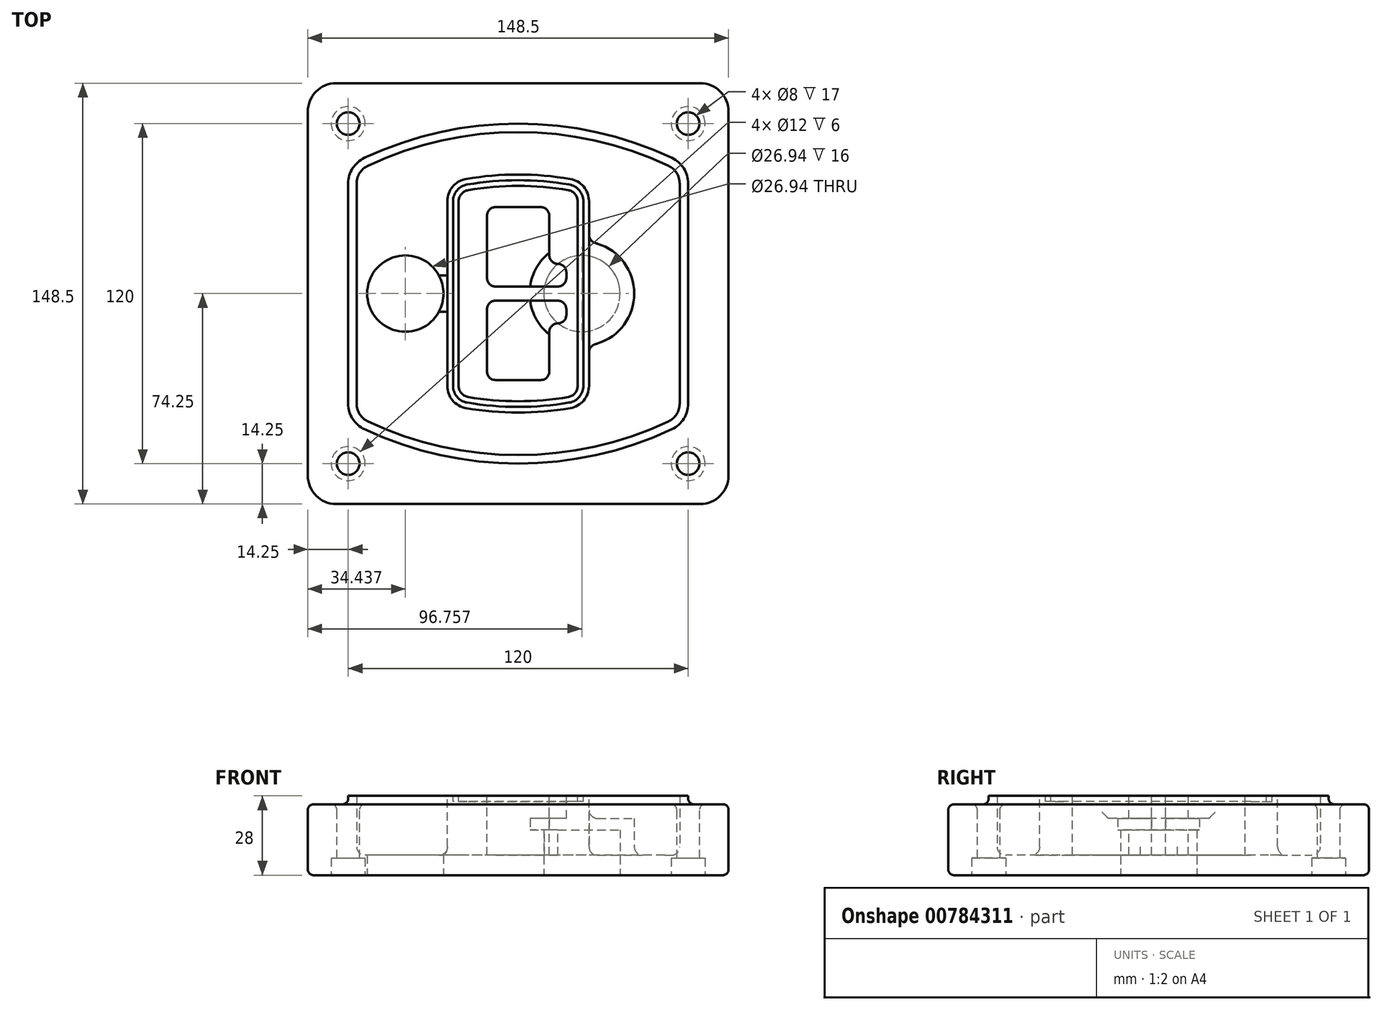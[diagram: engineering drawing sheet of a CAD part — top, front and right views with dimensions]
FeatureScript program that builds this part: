
annotation { "Feature Type Name" : "Feature", "Feature Type Description" : "" }
export const myFeature = defineFeature(function(context is Context, id is Id, definition is map)
    precondition{}
    {
        {
            var Q0;
            Q0=qCreatedBy(makeId("Top.planeOp"),FACE);
            var sketch = newSketch(context, id + "F0", { "sketchPlane" : qUnion([Q0])});
            skPoint(sketch, "E0.rect.middle", {"position": v(0, 0) * mm});
            skLineSegment(sketch, "E1.bottom", {"start": v(-64.25, -74.25) * mm, "end": v(64.25, -74.25) * mm});
            skLineSegment(sketch, "E1.top", {"start": v(-64.25, 74.25) * mm, "end": v(64.25, 74.25) * mm});
            skLineSegment(sketch, "E1.left", {"start": v(-74.25, -64.25) * mm, "end": v(-74.25, 64.25) * mm});
            skLineSegment(sketch, "E1.right", {"start": v(74.25, -64.25) * mm, "end": v(74.25, 64.25) * mm});
            skLineSegment(sketch, "E2", {"start": v(-74.25, 74.25) * mm, "end": v(74.25, -74.25) * mm, "construction": true});
            skLineSegment(sketch, "E3", {"start": v(74.25, 74.25) * mm, "end": v(-74.25, -74.25) * mm, "construction": true});
            skCircle(sketch, "E4", {"center": v(-60, 60) * mm, "radius": 4 * mm});
            skCircle(sketch, "E5", {"center": v(60, 60) * mm, "radius": 4 * mm});
            skCircle(sketch, "E6", {"center": v(60, -60) * mm, "radius": 4 * mm});
            skCircle(sketch, "E7", {"center": v(-60, -60) * mm, "radius": 4 * mm});
            skLineSegment(sketch, "E8", {"start": v(-60, 60) * mm, "end": v(60, 60) * mm, "construction": true});
            skLineSegment(sketch, "E9", {"start": v(60, 60) * mm, "end": v(60, -60) * mm, "construction": true});
            skLineSegment(sketch, "E10", {"start": v(60, -60) * mm, "end": v(-60, -60) * mm, "construction": true});
            skLineSegment(sketch, "E11", {"start": v(-60, -60) * mm, "end": v(-60, 60) * mm, "construction": true});
            skLineSegment(sketch, "E12", {"start": v(-60, 38.83) * mm, "end": v(-60, -38.83) * mm});
            skLineSegment(sketch, "E13", {"start": v(60, 38.83) * mm, "end": v(60, -38.83) * mm});
            skArc(sketch, "E14", {"start": v(54.26, 47.88) * mm, "mid": v(0, 60) * mm, "end": v(-54.26, 47.88) * mm});
            skArc(sketch, "E15", {"start": v(-54.26, -47.88) * mm, "mid": v(0, -60) * mm, "end": v(54.26, -47.88) * mm});
            skLineSegment(sketch, "E16", {"start": v(-60, 0) * mm, "end": v(60, 0) * mm, "construction": true});
            skPoint(sketch, "E17.visualSharp", {"position": v(-60, -45) * mm});
            skArc(sketch, "E17.filletArc", {"start": v(-60, -38.83) * mm, "mid": v(-58.44, -44.2) * mm, "end": v(-54.26, -47.88) * mm});
            skPoint(sketch, "E18.visualSharp", {"position": v(-60, 45) * mm});
            skArc(sketch, "E18.filletArc", {"start": v(-54.26, 47.88) * mm, "mid": v(-58.44, 44.2) * mm, "end": v(-60, 38.83) * mm});
            skPoint(sketch, "E19.visualSharp", {"position": v(60, 45) * mm});
            skArc(sketch, "E19.filletArc", {"start": v(60, 38.83) * mm, "mid": v(58.44, 44.2) * mm, "end": v(54.26, 47.88) * mm});
            skPoint(sketch, "E20.visualSharp", {"position": v(60, -45) * mm});
            skArc(sketch, "E20.filletArc", {"start": v(54.26, -47.88) * mm, "mid": v(58.44, -44.2) * mm, "end": v(60, -38.83) * mm});
            skPoint(sketch, "E21.visualSharp", {"position": v(-74.25, 74.25) * mm});
            skArc(sketch, "E21.filletArc", {"start": v(-64.25, 74.25) * mm, "mid": v(-71.32, 71.32) * mm, "end": v(-74.25, 64.25) * mm});
            skPoint(sketch, "E22.visualSharp", {"position": v(74.25, 74.25) * mm});
            skArc(sketch, "E22.filletArc", {"start": v(74.25, 64.25) * mm, "mid": v(71.32, 71.32) * mm, "end": v(64.25, 74.25) * mm});
            skPoint(sketch, "E23.visualSharp", {"position": v(74.25, -74.25) * mm});
            skArc(sketch, "E23.filletArc", {"start": v(64.25, -74.25) * mm, "mid": v(71.32, -71.32) * mm, "end": v(74.25, -64.25) * mm});
            skPoint(sketch, "E24.visualSharp", {"position": v(-74.25, -74.25) * mm});
            skArc(sketch, "E24.filletArc", {"start": v(-74.25, -64.25) * mm, "mid": v(-71.32, -71.32) * mm, "end": v(-64.25, -74.25) * mm});
            skArc(sketch, "E25.0", {"start": v(57, 38.83) * mm, "mid": v(55.9, 42.58) * mm, "end": v(52.98, 45.17) * mm});
            skLineSegment(sketch, "E25.1", {"start": v(57, 38.83) * mm, "end": v(57, -38.83) * mm});
            skArc(sketch, "E25.2", {"start": v(52.98, -45.17) * mm, "mid": v(55.9, -42.58) * mm, "end": v(57, -38.83) * mm});
            skArc(sketch, "E25.3", {"start": v(-52.98, -45.17) * mm, "mid": v(0, -57) * mm, "end": v(52.98, -45.17) * mm});
            skArc(sketch, "E25.4", {"start": v(-57, -38.83) * mm, "mid": v(-55.9, -42.58) * mm, "end": v(-52.98, -45.17) * mm});
            skArc(sketch, "E25.5", {"start": v(52.98, 45.17) * mm, "mid": v(0, 57) * mm, "end": v(-52.98, 45.17) * mm});
            skLineSegment(sketch, "E25.6", {"start": v(-57, 38.83) * mm, "end": v(-57, -38.83) * mm});
            skArc(sketch, "E25.7", {"start": v(-52.98, 45.17) * mm, "mid": v(-55.9, 42.58) * mm, "end": v(-57, 38.83) * mm});
            skArc(sketch, "E26.0", {"start": v(-55.96, 51.5) * mm, "mid": v(-61.82, 46.33) * mm, "end": v(-64, 38.83) * mm});
            skArc(sketch, "E26.1", {"start": v(55.96, 51.5) * mm, "mid": v(0, 64) * mm, "end": v(-55.96, 51.5) * mm});
            skArc(sketch, "E26.2", {"start": v(64, 38.83) * mm, "mid": v(61.82, 46.33) * mm, "end": v(55.96, 51.5) * mm});
            skLineSegment(sketch, "E26.3", {"start": v(64, 38.83) * mm, "end": v(64, -38.83) * mm});
            skArc(sketch, "E26.4", {"start": v(55.96, -51.5) * mm, "mid": v(61.82, -46.33) * mm, "end": v(64, -38.83) * mm});
            skLineSegment(sketch, "E26.5", {"start": v(-64, 38.83) * mm, "end": v(-64, -38.83) * mm});
            skArc(sketch, "E26.6", {"start": v(-55.96, -51.5) * mm, "mid": v(0, -64) * mm, "end": v(55.96, -51.5) * mm});
            skArc(sketch, "E26.7", {"start": v(-64, -38.83) * mm, "mid": v(-61.82, -46.33) * mm, "end": v(-55.96, -51.5) * mm});
            skSolve(sketch);
        }
        {
            var Q0;
            Q0=makeQuery(id+"F0.imprint","IMPRINT",FACE,{"disambiguationData":[TD([[makeQuery(id+"F0.imprint","IMPRINT",EDGE,{"derivedFrom":sQuery(id+"F0.wireOp",EDGE,"E1.bottom")}),1.0]])]});
            var Q1;
            Q1=makeQuery(id+"F0.imprint","IMPRINT",FACE,{"disambiguationData":[TD([[makeQuery(id+"F0.imprint","IMPRINT",EDGE,{"derivedFrom":sQuery(id+"F0.wireOp",EDGE,"E12")}),1.0]])]});
            var Q2;
            Q2=makeQuery(id+"F0.imprint","IMPRINT",FACE,{"disambiguationData":[TD([[makeQuery(id+"F0.imprint","IMPRINT",EDGE,{"derivedFrom":sQuery(id+"F0.wireOp",EDGE,"E25.0")}),1.0]])]});
            var Q3;
            Q3=makeQuery(id+"F0.imprint","IMPRINT",FACE,{"disambiguationData":[TD([[makeQuery(id+"F0.imprint","IMPRINT",EDGE,{"derivedFrom":sQuery(id+"F0.wireOp",EDGE,"E12")}),-1.0]])]});
            extrude(context, id + "F1", {"entities" : qUnion([Q0, Q1, Q2, Q3]), "oppositeDirection" : true, "depth" : 25 * mm});
        }
        {
            var Q0;
            Q0=makeQuery(id+"F0.imprint","IMPRINT",FACE,{"disambiguationData":[TD([[makeQuery(id+"F0.imprint","IMPRINT",EDGE,{"derivedFrom":sQuery(id+"F0.wireOp",EDGE,"E12")}),1.0]])]});
            extrude(context, id + "F2", {"entities" : qUnion([Q0]), "operationType" : NewBodyOperationType.ADD, "depth" : 3 * mm});
        }
        {
            var Q0;
            Q0=makeQuery(id+"F0.imprint","IMPRINT",FACE,{"disambiguationData":[TD([[makeQuery(id+"F0.imprint","IMPRINT",EDGE,{"derivedFrom":sQuery(id+"F0.wireOp",EDGE,"E25.0")}),1.0]])]});
            extrude(context, id + "F3", {"entities" : qUnion([Q0]), "operationType" : NewBodyOperationType.REMOVE, "oppositeDirection" : true, "depth" : 18 * mm});
        }
        {
            var Q0;
            Q0=makeQuery(id+"F2.opExtrude","CAP_FACE",FACE,{"disambiguationData":[OSD([sQuery(id+"F0.wireOp",EDGE,"E12"),sQuery(id+"F0.wireOp",EDGE,"E13"),sQuery(id+"F0.wireOp",EDGE,"E14"),sQuery(id+"F0.wireOp",EDGE,"E15"),sQuery(id+"F0.wireOp",EDGE,"E17.filletArc"),sQuery(id+"F0.wireOp",EDGE,"E18.filletArc"),sQuery(id+"F0.wireOp",EDGE,"E19.filletArc"),sQuery(id+"F0.wireOp",EDGE,"E20.filletArc"),sQuery(id+"F0.wireOp",EDGE,"E25.0"),sQuery(id+"F0.wireOp",EDGE,"E25.1"),sQuery(id+"F0.wireOp",EDGE,"E25.2"),sQuery(id+"F0.wireOp",EDGE,"E25.3"),sQuery(id+"F0.wireOp",EDGE,"E25.4"),sQuery(id+"F0.wireOp",EDGE,"E25.5"),sQuery(id+"F0.wireOp",EDGE,"E25.6"),sQuery(id+"F0.wireOp",EDGE,"E25.7")])],"isStart":false});
            var sketch = newSketch(context, id + "F4", { "sketchPlane" : qUnion([Q0])});
            skArc(sketch, "E27.0", {"start": v(-18.34, -40.45) * mm, "mid": v(0, -42) * mm, "end": v(18.34, -40.45) * mm});
            skArc(sketch, "E28.0", {"start": v(18.34, 40.45) * mm, "mid": v(0, 42) * mm, "end": v(-18.34, 40.45) * mm});
            skLineSegment(sketch, "E29", {"start": v(-25, 32.57) * mm, "end": v(-25, -32.57) * mm});
            skLineSegment(sketch, "E30", {"start": v(25, 32.57) * mm, "end": v(25, -32.57) * mm});
            skLineSegment(sketch, "E31", {"start": v(-25, 39.1) * mm, "end": v(25, 39.1) * mm, "construction": true});
            skLineSegment(sketch, "E32", {"start": v(-25, -39.1) * mm, "end": v(25, -39.1) * mm, "construction": true});
            skPoint(sketch, "E33.visualSharp", {"position": v(-25, 39.1) * mm});
            skArc(sketch, "E33.filletArc", {"start": v(-18.34, 40.45) * mm, "mid": v(-23.11, 37.73) * mm, "end": v(-25, 32.57) * mm});
            skPoint(sketch, "E34.visualSharp", {"position": v(25, 39.1) * mm});
            skArc(sketch, "E34.filletArc", {"start": v(25, 32.57) * mm, "mid": v(23.11, 37.73) * mm, "end": v(18.34, 40.45) * mm});
            skPoint(sketch, "E35.visualSharp", {"position": v(25, -39.1) * mm});
            skArc(sketch, "E35.filletArc", {"start": v(18.34, -40.45) * mm, "mid": v(23.11, -37.73) * mm, "end": v(25, -32.57) * mm});
            skPoint(sketch, "E36.visualSharp", {"position": v(-25, -39.1) * mm});
            skArc(sketch, "E36.filletArc", {"start": v(-25, -32.57) * mm, "mid": v(-23.11, -37.73) * mm, "end": v(-18.34, -40.45) * mm});
            skArc(sketch, "E37.0", {"start": v(52.98, 45.17) * mm, "mid": v(0, 57) * mm, "end": v(-52.98, 45.17) * mm});
            skArc(sketch, "E37.1", {"start": v(-52.98, 45.17) * mm, "mid": v(-55.9, 42.58) * mm, "end": v(-57, 38.83) * mm});
            skLineSegment(sketch, "E37.2", {"start": v(-57, 38.83) * mm, "end": v(-57, -38.83) * mm});
            skArc(sketch, "E37.3", {"start": v(-57, -38.83) * mm, "mid": v(-55.9, -42.58) * mm, "end": v(-52.98, -45.17) * mm});
            skArc(sketch, "E37.4", {"start": v(-52.98, -45.17) * mm, "mid": v(0, -57) * mm, "end": v(52.98, -45.17) * mm});
            skArc(sketch, "E37.5", {"start": v(52.98, -45.17) * mm, "mid": v(55.9, -42.58) * mm, "end": v(57, -38.83) * mm});
            skLineSegment(sketch, "E37.6", {"start": v(57, 38.83) * mm, "end": v(57, -38.83) * mm});
            skArc(sketch, "E37.7", {"start": v(57, 38.83) * mm, "mid": v(55.9, 42.58) * mm, "end": v(52.98, 45.17) * mm});
            skLineSegment(sketch, "E38.0", {"start": v(23, 32.57) * mm, "end": v(23, -32.57) * mm});
            skArc(sketch, "E38.1", {"start": v(18, -38.48) * mm, "mid": v(21.58, -36.44) * mm, "end": v(23, -32.57) * mm});
            skArc(sketch, "E38.2", {"start": v(-18, -38.48) * mm, "mid": v(0, -40) * mm, "end": v(18, -38.48) * mm});
            skArc(sketch, "E38.3", {"start": v(-23, -32.57) * mm, "mid": v(-21.58, -36.44) * mm, "end": v(-18, -38.48) * mm});
            skLineSegment(sketch, "E38.4", {"start": v(-23, 32.57) * mm, "end": v(-23, -32.57) * mm});
            skArc(sketch, "E38.5", {"start": v(23, 32.57) * mm, "mid": v(21.58, 36.44) * mm, "end": v(18, 38.48) * mm});
            skArc(sketch, "E38.6", {"start": v(-18, 38.48) * mm, "mid": v(-21.58, 36.44) * mm, "end": v(-23, 32.57) * mm});
            skArc(sketch, "E38.7", {"start": v(18, 38.48) * mm, "mid": v(0, 40) * mm, "end": v(-18, 38.48) * mm});
            skArc(sketch, "E39.0", {"start": v(21, 32.57) * mm, "mid": v(20.06, 35.15) * mm, "end": v(17.67, 36.5) * mm});
            skLineSegment(sketch, "E39.1", {"start": v(21, 32.57) * mm, "end": v(21, -32.57) * mm});
            skArc(sketch, "E39.2", {"start": v(17.67, -36.5) * mm, "mid": v(20.06, -35.15) * mm, "end": v(21, -32.57) * mm});
            skArc(sketch, "E39.3", {"start": v(-17.67, -36.5) * mm, "mid": v(0, -38) * mm, "end": v(17.67, -36.5) * mm});
            skArc(sketch, "E39.4", {"start": v(-21, -32.57) * mm, "mid": v(-20.06, -35.15) * mm, "end": v(-17.67, -36.5) * mm});
            skArc(sketch, "E39.5", {"start": v(17.67, 36.5) * mm, "mid": v(0, 38) * mm, "end": v(-17.67, 36.5) * mm});
            skLineSegment(sketch, "E39.6", {"start": v(-21, 32.57) * mm, "end": v(-21, -32.57) * mm});
            skArc(sketch, "E39.7", {"start": v(-17.67, 36.5) * mm, "mid": v(-20.06, 35.15) * mm, "end": v(-21, 32.57) * mm});
            skLineSegment(sketch, "E40", {"start": v(-25, 0) * mm, "end": v(25, 0) * mm, "construction": true});
            skLineSegment(sketch, "E41", {"start": v(-11, 5.5) * mm, "end": v(-11, 27.5) * mm});
            skLineSegment(sketch, "E42", {"start": v(-8, 30.5) * mm, "end": v(8, 30.5) * mm});
            skLineSegment(sketch, "E43", {"start": v(11, 27.5) * mm, "end": v(11, 13.5) * mm});
            skLineSegment(sketch, "E44", {"start": v(14, 10.5) * mm, "end": v(14, 10.5) * mm});
            skLineSegment(sketch, "E45", {"start": v(17, 7.5) * mm, "end": v(17, 5.5) * mm});
            skLineSegment(sketch, "E46", {"start": v(14, 2.5) * mm, "end": v(-8, 2.5) * mm});
            skPoint(sketch, "E47.visualSharp", {"position": v(-11, 30.5) * mm});
            skArc(sketch, "E47.filletArc", {"start": v(-8, 30.5) * mm, "mid": v(-10.12, 29.62) * mm, "end": v(-11, 27.5) * mm});
            skPoint(sketch, "E48.visualSharp", {"position": v(11, 30.5) * mm});
            skArc(sketch, "E48.filletArc", {"start": v(11, 27.5) * mm, "mid": v(10.12, 29.62) * mm, "end": v(8, 30.5) * mm});
            skPoint(sketch, "E49.visualSharp", {"position": v(11, 10.5) * mm});
            skArc(sketch, "E49.filletArc", {"start": v(11, 13.5) * mm, "mid": v(11.88, 11.38) * mm, "end": v(14, 10.5) * mm});
            skPoint(sketch, "E50.visualSharp", {"position": v(17, 10.5) * mm});
            skArc(sketch, "E50.filletArc", {"start": v(17, 7.5) * mm, "mid": v(16.12, 9.62) * mm, "end": v(14, 10.5) * mm});
            skPoint(sketch, "E51.visualSharp", {"position": v(17, 2.5) * mm});
            skArc(sketch, "E51.filletArc", {"start": v(14, 2.5) * mm, "mid": v(16.12, 3.38) * mm, "end": v(17, 5.5) * mm});
            skPoint(sketch, "E52.visualSharp", {"position": v(-11, 2.5) * mm});
            skArc(sketch, "E52.filletArc", {"start": v(-11, 5.5) * mm, "mid": v(-10.12, 3.38) * mm, "end": v(-8, 2.5) * mm});
            skLineSegment(sketch, "E53.0.MirrorCS", {"start": v(14, -2.5) * mm, "end": v(-8, -2.5) * mm});
            skArc(sketch, "E54.0.MirrorCS", {"start": v(-11, -5.5) * mm, "mid": v(-10.12, -3.38) * mm, "end": v(-8, -2.5) * mm});
            skLineSegment(sketch, "E55.0.MirrorCS", {"start": v(-11, -5.5) * mm, "end": v(-11, -27.5) * mm});
            skArc(sketch, "E56.0.MirrorCS", {"start": v(-8, -30.5) * mm, "mid": v(-10.12, -29.62) * mm, "end": v(-11, -27.5) * mm});
            skLineSegment(sketch, "E57.0.MirrorCS", {"start": v(-8, -30.5) * mm, "end": v(8, -30.5) * mm});
            skArc(sketch, "E58.0.MirrorCS", {"start": v(11, -27.5) * mm, "mid": v(10.12, -29.62) * mm, "end": v(8, -30.5) * mm});
            skLineSegment(sketch, "E59.0.MirrorCS", {"start": v(11, -27.5) * mm, "end": v(11, -13.5) * mm});
            skArc(sketch, "E60.0.MirrorCS", {"start": v(11, -13.5) * mm, "mid": v(11.88, -11.38) * mm, "end": v(14, -10.5) * mm});
            skArc(sketch, "E61.0.MirrorCS", {"start": v(17, -7.5) * mm, "mid": v(16.12, -9.62) * mm, "end": v(14, -10.5) * mm});
            skLineSegment(sketch, "E62.0.MirrorCS", {"start": v(17, -7.5) * mm, "end": v(17, -5.5) * mm});
            skArc(sketch, "E63.0.MirrorCS", {"start": v(14, -2.5) * mm, "mid": v(16.12, -3.38) * mm, "end": v(17, -5.5) * mm});
            skSolve(sketch);
        }
        {
            var Q0;
            Q0=makeQuery(id+"F4.imprint","IMPRINT",FACE,{"disambiguationData":[TD([[makeQuery(id+"F4.imprint","IMPRINT",EDGE,{"derivedFrom":sQuery(id+"F4.wireOp",EDGE,"E27.0")}),1.0]])]});
            var Q1;
            Q1=makeQuery(id+"F4.imprint","IMPRINT",FACE,{"disambiguationData":[TD([[makeQuery(id+"F4.imprint","IMPRINT",EDGE,{"derivedFrom":sQuery(id+"F4.wireOp",EDGE,"E38.0")}),-1.0]])]});
            var Q2;
            Q2=makeQuery(id+"F4.imprint","IMPRINT",FACE,{"disambiguationData":[TD([[makeQuery(id+"F4.imprint","IMPRINT",EDGE,{"derivedFrom":sQuery(id+"F4.wireOp",EDGE,"E39.0")}),1.0]])]});
            extrude(context, id + "F5", {"entities" : qUnion([Q0, Q1, Q2]), "operationType" : NewBodyOperationType.ADD, "endBound" : BoundingType.UP_TO_NEXT, "oppositeDirection" : true, "depth" : 25 * mm});
        }
        {
            var Q0;
            Q0=makeQuery(id+"F4.imprint","IMPRINT",FACE,{"disambiguationData":[TD([[makeQuery(id+"F4.imprint","IMPRINT",EDGE,{"derivedFrom":sQuery(id+"F4.wireOp",EDGE,"E38.0")}),-1.0]])]});
            extrude(context, id + "F6", {"entities" : qUnion([Q0]), "operationType" : NewBodyOperationType.REMOVE, "oppositeDirection" : true, "depth" : 2 * mm});
        }
        {
            var Q0;
            Q0=makeQuery(id+"F1.opExtrude","CAP_FACE",FACE,{"disambiguationData":[OSD([sQuery(id+"F0.wireOp",EDGE,"E1.bottom"),sQuery(id+"F0.wireOp",EDGE,"E1.top"),sQuery(id+"F0.wireOp",EDGE,"E1.left"),sQuery(id+"F0.wireOp",EDGE,"E1.right"),sQuery(id+"F0.wireOp",EDGE,"E4"),sQuery(id+"F0.wireOp",EDGE,"E5"),sQuery(id+"F0.wireOp",EDGE,"E6"),sQuery(id+"F0.wireOp",EDGE,"E7"),sQuery(id+"F0.wireOp",EDGE,"E21.filletArc"),sQuery(id+"F0.wireOp",EDGE,"E22.filletArc"),sQuery(id+"F0.wireOp",EDGE,"E23.filletArc"),sQuery(id+"F0.wireOp",EDGE,"E24.filletArc")])],"isStart":false});
            var sketch = newSketch(context, id + "F7", { "sketchPlane" : qUnion([Q0])});
            skCircle(sketch, "E64", {"center": v(22.5, 0) * mm, "radius": 13.47 * mm});
            skCircle(sketch, "E65", {"center": v(-39.81, 0) * mm, "radius": 13.47 * mm});
            skLineSegment(sketch, "E66", {"start": v(74.25, 0) * mm, "end": v(-74.25, 0) * mm});
            skCircle(sketch, "E67", {"center": v(22.5, 0) * mm, "radius": 18.47 * mm});
            skCircle(sketch, "E68", {"center": v(60, -60) * mm, "radius": 6 * mm});
            skCircle(sketch, "E69", {"center": v(-60, -60) * mm, "radius": 6 * mm});
            skCircle(sketch, "E70", {"center": v(-60, 60) * mm, "radius": 6 * mm});
            skCircle(sketch, "E71", {"center": v(60, 60) * mm, "radius": 6 * mm});
            skSolve(sketch);
        }
        {
            var Q0;
            {var subQ1=sQuery(id+"F7.wireOp",EDGE,"E66");var subQ4=sQuery(id+"F7.wireOp",EDGE,"E64");var subQ6=makeQuery(id+"F7.imprint","INTERSECT",VERTEX,{"disambiguationData":[OD(0.0)],"derivedFrom":[subQ4,subQ1]});Q0=makeQuery(id+"F7.imprint","IMPRINT",FACE,{"disambiguationData":[TD([[makeQuery(id+"F7.imprint","IMPRINT",EDGE,{"disambiguationData":[TD([[subQ6,-1.0]])],"derivedFrom":subQ4}),-1.0]])]});}
            var Q1;
            {var subQ0=sQuery(id+"F7.wireOp",EDGE,"E66");var subQ1=sQuery(id+"F7.wireOp",EDGE,"E64");var subQ3=makeQuery(id+"F7.imprint","INTERSECT",VERTEX,{"disambiguationData":[OD(0.0)],"derivedFrom":[subQ1,subQ0]});Q1=makeQuery(id+"F7.imprint","IMPRINT",FACE,{"disambiguationData":[TD([[makeQuery(id+"F7.imprint","IMPRINT",EDGE,{"disambiguationData":[TD([[subQ3,-1.0]])],"derivedFrom":subQ1}),1.0]])]});}
            var Q2;
            {var subQ0=sQuery(id+"F7.wireOp",EDGE,"E66");var subQ1=sQuery(id+"F7.wireOp",EDGE,"E64");var subQ3=makeQuery(id+"F7.imprint","INTERSECT",VERTEX,{"disambiguationData":[OD(0.0)],"derivedFrom":[subQ1,subQ0]});Q2=makeQuery(id+"F7.imprint","IMPRINT",FACE,{"disambiguationData":[TD([[makeQuery(id+"F7.imprint","IMPRINT",EDGE,{"disambiguationData":[TD([[subQ3,1.0]])],"derivedFrom":subQ1}),1.0]])]});}
            var Q3;
            {var subQ1=sQuery(id+"F7.wireOp",EDGE,"E66");var subQ4=sQuery(id+"F7.wireOp",EDGE,"E64");var subQ6=makeQuery(id+"F7.imprint","INTERSECT",VERTEX,{"disambiguationData":[OD(0.0)],"derivedFrom":[subQ4,subQ1]});Q3=makeQuery(id+"F7.imprint","IMPRINT",FACE,{"disambiguationData":[TD([[makeQuery(id+"F7.imprint","IMPRINT",EDGE,{"disambiguationData":[TD([[subQ6,1.0]])],"derivedFrom":subQ4}),-1.0]])]});}
            extrude(context, id + "F8", {"entities" : qUnion([Q0, Q1, Q2, Q3]), "operationType" : NewBodyOperationType.ADD, "oppositeDirection" : true, "depth" : 20 * mm});
        }
        {
            var Q0;
            {var subQ0=sQuery(id+"F7.wireOp",EDGE,"E66");var subQ1=sQuery(id+"F7.wireOp",EDGE,"E64");var subQ3=makeQuery(id+"F7.imprint","INTERSECT",VERTEX,{"disambiguationData":[OD(0.0)],"derivedFrom":[subQ1,subQ0]});Q0=makeQuery(id+"F7.imprint","IMPRINT",FACE,{"disambiguationData":[TD([[makeQuery(id+"F7.imprint","IMPRINT",EDGE,{"disambiguationData":[TD([[subQ3,-1.0]])],"derivedFrom":subQ1}),1.0]])]});}
            var Q1;
            {var subQ0=sQuery(id+"F7.wireOp",EDGE,"E66");var subQ1=sQuery(id+"F7.wireOp",EDGE,"E64");var subQ3=makeQuery(id+"F7.imprint","INTERSECT",VERTEX,{"disambiguationData":[OD(0.0)],"derivedFrom":[subQ1,subQ0]});Q1=makeQuery(id+"F7.imprint","IMPRINT",FACE,{"disambiguationData":[TD([[makeQuery(id+"F7.imprint","IMPRINT",EDGE,{"disambiguationData":[TD([[subQ3,1.0]])],"derivedFrom":subQ1}),1.0]])]});}
            extrude(context, id + "F9", {"entities" : qUnion([Q0, Q1]), "operationType" : NewBodyOperationType.REMOVE, "oppositeDirection" : true, "depth" : 16 * mm});
        }
        {
            var Q0;
            {var subQ0=sQuery(id+"F7.wireOp",EDGE,"E66");var subQ1=sQuery(id+"F7.wireOp",EDGE,"E65");var subQ3=makeQuery(id+"F7.imprint","INTERSECT",VERTEX,{"disambiguationData":[OD(0.0)],"derivedFrom":[subQ1,subQ0]});Q0=makeQuery(id+"F7.imprint","IMPRINT",FACE,{"disambiguationData":[TD([[makeQuery(id+"F7.imprint","IMPRINT",EDGE,{"disambiguationData":[TD([[subQ3,-1.0]])],"derivedFrom":subQ1}),1.0]])]});}
            var Q1;
            {var subQ0=sQuery(id+"F7.wireOp",EDGE,"E66");var subQ1=sQuery(id+"F7.wireOp",EDGE,"E65");var subQ3=makeQuery(id+"F7.imprint","INTERSECT",VERTEX,{"disambiguationData":[OD(0.0)],"derivedFrom":[subQ1,subQ0]});Q1=makeQuery(id+"F7.imprint","IMPRINT",FACE,{"disambiguationData":[TD([[makeQuery(id+"F7.imprint","IMPRINT",EDGE,{"disambiguationData":[TD([[subQ3,1.0]])],"derivedFrom":subQ1}),1.0]])]});}
            extrude(context, id + "F10", {"entities" : qUnion([Q0, Q1]), "operationType" : NewBodyOperationType.REMOVE, "oppositeDirection" : true, "depth" : 25 * mm});
        }
        {
            var Q0;
            Q0=makeQuery(id+"F7.imprint","IMPRINT",FACE,{"disambiguationData":[TD([[makeQuery(id+"F7.imprint","IMPRINT",EDGE,{"derivedFrom":sQuery(id+"F7.wireOp",EDGE,"E68")}),1.0]])]});
            var Q1;
            Q1=makeQuery(id+"F7.imprint","IMPRINT",FACE,{"disambiguationData":[TD([[makeQuery(id+"F7.imprint","IMPRINT",EDGE,{"derivedFrom":makeQuery(id+"F1.opExtrude","CAP_EDGE",EDGE,{"disambiguationData":[OSD([sQuery(id+"F0.wireOp",EDGE,"E5")])],"isStart":false})}),-1.0]])]});
            var Q2;
            Q2=makeQuery(id+"F7.imprint","IMPRINT",FACE,{"disambiguationData":[TD([[makeQuery(id+"F7.imprint","IMPRINT",EDGE,{"derivedFrom":sQuery(id+"F7.wireOp",EDGE,"E69")}),1.0]])]});
            var Q3;
            Q3=makeQuery(id+"F7.imprint","IMPRINT",FACE,{"disambiguationData":[TD([[makeQuery(id+"F7.imprint","IMPRINT",EDGE,{"derivedFrom":makeQuery(id+"F1.opExtrude","CAP_EDGE",EDGE,{"disambiguationData":[OSD([sQuery(id+"F0.wireOp",EDGE,"E4")])],"isStart":false})}),-1.0]])]});
            var Q4;
            Q4=makeQuery(id+"F7.imprint","IMPRINT",FACE,{"disambiguationData":[TD([[makeQuery(id+"F7.imprint","IMPRINT",EDGE,{"derivedFrom":sQuery(id+"F7.wireOp",EDGE,"E70")}),1.0]])]});
            var Q5;
            Q5=makeQuery(id+"F7.imprint","IMPRINT",FACE,{"disambiguationData":[TD([[makeQuery(id+"F7.imprint","IMPRINT",EDGE,{"derivedFrom":makeQuery(id+"F1.opExtrude","CAP_EDGE",EDGE,{"disambiguationData":[OSD([sQuery(id+"F0.wireOp",EDGE,"E7")])],"isStart":false})}),-1.0]])]});
            var Q6;
            Q6=makeQuery(id+"F7.imprint","IMPRINT",FACE,{"disambiguationData":[TD([[makeQuery(id+"F7.imprint","IMPRINT",EDGE,{"derivedFrom":sQuery(id+"F7.wireOp",EDGE,"E71")}),1.0]])]});
            var Q7;
            Q7=makeQuery(id+"F7.imprint","IMPRINT",FACE,{"disambiguationData":[TD([[makeQuery(id+"F7.imprint","IMPRINT",EDGE,{"derivedFrom":makeQuery(id+"F1.opExtrude","CAP_EDGE",EDGE,{"disambiguationData":[OSD([sQuery(id+"F0.wireOp",EDGE,"E6")])],"isStart":false})}),-1.0]])]});
            extrude(context, id + "F11", {"entities" : qUnion([Q0, Q1, Q2, Q3, Q4, Q5, Q6, Q7]), "operationType" : NewBodyOperationType.REMOVE, "oppositeDirection" : true, "depth" : 6 * mm});
        }
        {
            var Q0;
            Q0=makeQuery(id+"F9.boolean.opBoolean","COPY",FACE,{"derivedFrom":makeQuery(id+"F9.opExtrude","CAP_FACE",FACE,{"disambiguationData":[OSD([sQuery(id+"F7.wireOp",EDGE,"E64")])],"isStart":false})});
            var sketch = newSketch(context, id + "F12", { "sketchPlane" : qUnion([Q0])});
            skArc(sketch, "E72.0", {"start": v(11, 14.45) * mm, "mid": v(6.45, 9.13) * mm, "end": v(4.2, 2.5) * mm});
            skArc(sketch, "E72.1", {"start": v(4.2, -2.5) * mm, "mid": v(6.45, -9.13) * mm, "end": v(11, -14.45) * mm});
            skLineSegment(sketch, "E73", {"start": v(4.2, -2.5) * mm, "end": v(14, -2.5) * mm});
            skLineSegment(sketch, "E74.0", {"start": v(14, 2.5) * mm, "end": v(4.2, 2.5) * mm});
            skArc(sketch, "E74.1", {"start": v(14, 2.5) * mm, "mid": v(16.12, 3.38) * mm, "end": v(17, 5.5) * mm});
            skLineSegment(sketch, "E74.2", {"start": v(17, 7.5) * mm, "end": v(17, 5.5) * mm});
            skArc(sketch, "E74.3", {"start": v(17, 7.5) * mm, "mid": v(16.12, 9.62) * mm, "end": v(14, 10.5) * mm});
            skArc(sketch, "E74.4", {"start": v(11, 13.5) * mm, "mid": v(11.88, 11.38) * mm, "end": v(14, 10.5) * mm});
            skLineSegment(sketch, "E74.5", {"start": v(11, 14.45) * mm, "end": v(11, 13.5) * mm});
            skLineSegment(sketch, "E74.7", {"start": v(14, -2.5) * mm, "end": v(4.2, -2.5) * mm});
            skArc(sketch, "E74.8", {"start": v(14, -2.5) * mm, "mid": v(16.12, -3.38) * mm, "end": v(17, -5.5) * mm});
            skLineSegment(sketch, "E74.9", {"start": v(17, -7.5) * mm, "end": v(17, -5.5) * mm});
            skArc(sketch, "E74.10", {"start": v(17, -7.5) * mm, "mid": v(16.12, -9.62) * mm, "end": v(14, -10.5) * mm});
            skArc(sketch, "E74.11", {"start": v(11, -13.5) * mm, "mid": v(11.88, -11.38) * mm, "end": v(14, -10.5) * mm});
            skLineSegment(sketch, "E74.12", {"start": v(11, -14.45) * mm, "end": v(11, -13.5) * mm});
            skPoint(sketch, "E75.orphan", {"position": v(11, -27.5) * mm});
            skPoint(sketch, "E76.orphan", {"position": v(-8, -2.5) * mm});
            skPoint(sketch, "E77.orphan", {"position": v(-8, 2.5) * mm});
            skPoint(sketch, "E78.orphan", {"position": v(11, 27.5) * mm});
            skSolve(sketch);
        }
        {
            var Q0;
            {var subQ7=sQuery(id+"F12.wireOp",EDGE,"E72.0");var subQ14=sQuery(id+"F12.wireOp",EDGE,"E72.1");var subQ16=sQuery(id+"F12.wireOp",EDGE,"E74.1");var subQ18=sQuery(id+"F12.wireOp",EDGE,"E74.8");Q0=qUnion([makeQuery(id+"F12.imprint","IMPRINT",FACE,{"disambiguationData":[TD([[makeQuery(id+"F12.imprint","IMPRINT",EDGE,{"derivedFrom":subQ7}),1.0]])]}),makeQuery(id+"F12.imprint","IMPRINT",FACE,{"disambiguationData":[TD([[makeQuery(id+"F12.imprint","IMPRINT",EDGE,{"derivedFrom":subQ14}),1.0]])]}),makeQuery(id+"F12.imprint","IMPRINT",FACE,{"disambiguationData":[TD([[makeQuery(id+"F12.imprint","IMPRINT",EDGE,{"derivedFrom":subQ16}),1.0]])]}),makeQuery(id+"F12.imprint","IMPRINT",FACE,{"disambiguationData":[TD([[makeQuery(id+"F12.imprint","IMPRINT",EDGE,{"derivedFrom":subQ18}),-1.0]])]})]);}
            var Q1;
            Q1=makeQuery(id+"F5.boolean.opBoolean","SPLIT",FACE,{"disambiguationData":[TD([makeQuery(id+"F5.opExtrude","SWEPT_FACE",FACE,{"disambiguationData":[OSD([sQuery(id+"F4.wireOp",EDGE,"E41")])]})])],"derivedFrom":makeQuery(id+"F3.boolean.opBoolean","COPY",FACE,{"derivedFrom":makeQuery(id+"F3.opExtrude","CAP_FACE",FACE,{"disambiguationData":[OSD([sQuery(id+"F0.wireOp",EDGE,"E25.0"),sQuery(id+"F0.wireOp",EDGE,"E25.1"),sQuery(id+"F0.wireOp",EDGE,"E25.2"),sQuery(id+"F0.wireOp",EDGE,"E25.3"),sQuery(id+"F0.wireOp",EDGE,"E25.4"),sQuery(id+"F0.wireOp",EDGE,"E25.5"),sQuery(id+"F0.wireOp",EDGE,"E25.6"),sQuery(id+"F0.wireOp",EDGE,"E25.7")])],"isStart":false})})});
            extrude(context, id + "F13", {"entities" : qUnion([Q0]), "operationType" : NewBodyOperationType.REMOVE, "endBound" : BoundingType.UP_TO_SURFACE, "endBoundEntityFace" : qUnion([Q1]), "depth" : 25 * mm});
        }
        {
            var Q0;
            Q0=makeQuery(id+"F3.boolean.opBoolean","COPY",EDGE,{"derivedFrom":makeQuery(id+"F3.opExtrude","CAP_EDGE",EDGE,{"disambiguationData":[OSD([sQuery(id+"F0.wireOp",EDGE,"E25.6")])],"isStart":false})});
            var Q1;
            Q1=makeQuery(id+"F8.boolean.opBoolean","INTERSECT",EDGE,{"derivedFrom":[makeQuery(id+"F5.opExtrude","SWEPT_FACE",FACE,{"disambiguationData":[OSD([sQuery(id+"F4.wireOp",EDGE,"E30")])]}),makeQuery(id+"F8.opExtrude","CAP_FACE",FACE,{"disambiguationData":[OSD([sQuery(id+"F7.wireOp",EDGE,"E67")])],"isStart":false})]});
            var Q2;
            Q2=makeQuery(id+"F8.boolean.opBoolean","INTERSECT",EDGE,{"disambiguationData":[OD(1.0)],"derivedFrom":[makeQuery(id+"F5.opExtrude","SWEPT_FACE",FACE,{"disambiguationData":[OSD([sQuery(id+"F4.wireOp",EDGE,"E30")])]}),makeQuery(id+"F8.opExtrude","SWEPT_FACE",FACE,{"disambiguationData":[OSD([sQuery(id+"F7.wireOp",EDGE,"E67")])]})]});
            var Q3;
            {var subQ0=sQuery(id+"F4.wireOp",EDGE,"E30");Q3=makeQuery(id+"F8.boolean.opBoolean","SPLIT",EDGE,{"disambiguationData":[TD([makeQuery(id+"F5.opExtrude","SWEPT_FACE",FACE,{"disambiguationData":[OSD([sQuery(id+"F4.wireOp",EDGE,"E35.filletArc")])]})])],"derivedFrom":makeQuery(id+"F5.opExtrude","CAP_EDGE",EDGE,{"disambiguationData":[OSD([subQ0])],"isStart":false})});}
            var Q4;
            {var subQ0=sQuery(id+"F0.wireOp",EDGE,"E25.7");var subQ1=sQuery(id+"F0.wireOp",EDGE,"E25.1");var subQ2=sQuery(id+"F0.wireOp",EDGE,"E25.6");var subQ3=sQuery(id+"F0.wireOp",EDGE,"E25.5");var subQ4=sQuery(id+"F0.wireOp",EDGE,"E25.4");var subQ5=sQuery(id+"F0.wireOp",EDGE,"E25.0");var subQ6=sQuery(id+"F0.wireOp",EDGE,"E25.2");var subQ7=sQuery(id+"F0.wireOp",EDGE,"E25.3");Q4=makeQuery(id+"F8.boolean.opBoolean","INTERSECT",EDGE,{"derivedFrom":[makeQuery(id+"F5.boolean.opBoolean","SPLIT",FACE,{"disambiguationData":[TD([makeQuery(id+"F2.opExtrude","SWEPT_FACE",FACE,{"disambiguationData":[OSD([subQ5])]})])],"derivedFrom":makeQuery(id+"F3.boolean.opBoolean","COPY",FACE,{"derivedFrom":makeQuery(id+"F3.opExtrude","CAP_FACE",FACE,{"disambiguationData":[OSD([subQ5,subQ1,subQ6,subQ7,subQ4,subQ3,subQ2,subQ0])],"isStart":false})})}),makeQuery(id+"F8.opExtrude","SWEPT_FACE",FACE,{"disambiguationData":[OSD([sQuery(id+"F7.wireOp",EDGE,"E67")])]})]});}
            var Q5;
            Q5=makeQuery(id+"F8.boolean.opBoolean","INTERSECT",EDGE,{"disambiguationData":[OD(0.0)],"derivedFrom":[makeQuery(id+"F5.opExtrude","SWEPT_FACE",FACE,{"disambiguationData":[OSD([sQuery(id+"F4.wireOp",EDGE,"E30")])]}),makeQuery(id+"F8.opExtrude","SWEPT_FACE",FACE,{"disambiguationData":[OSD([sQuery(id+"F7.wireOp",EDGE,"E67")])]})]});
            fillet(context, id + "F14", {"entities" : qUnion([Q0, Q1, Q2, Q3, Q4, Q5]), "radius" : 3 * mm, "tangentPropagation" : true, "allowEdgeOverflow" : false});
        }
        {
            var Q0;
            Q0=makeQuery(id+"F1.opExtrude","CAP_EDGE",EDGE,{"disambiguationData":[OSD([sQuery(id+"F0.wireOp",EDGE,"E1.bottom")])],"isStart":false});
            var Q1;
            {var subQ0=sQuery(id+"F0.wireOp",EDGE,"E21.filletArc");var subQ1=sQuery(id+"F0.wireOp",EDGE,"E7");var subQ2=sQuery(id+"F0.wireOp",EDGE,"E6");var subQ3=sQuery(id+"F0.wireOp",EDGE,"E5");var subQ4=sQuery(id+"F0.wireOp",EDGE,"E4");var subQ5=sQuery(id+"F0.wireOp",EDGE,"E22.filletArc");var subQ6=sQuery(id+"F0.wireOp",EDGE,"E1.bottom");var subQ7=sQuery(id+"F0.wireOp",EDGE,"E1.right");var subQ8=sQuery(id+"F0.wireOp",EDGE,"E1.top");var subQ9=sQuery(id+"F0.wireOp",EDGE,"E1.left");var subQ10=sQuery(id+"F0.wireOp",EDGE,"E23.filletArc");var subQ11=sQuery(id+"F0.wireOp",EDGE,"E24.filletArc");Q1=makeQuery(id+"F2.boolean.opBoolean","SPLIT",FACE,{"disambiguationData":[TD([makeQuery(id+"F1.opExtrude","SWEPT_FACE",FACE,{"disambiguationData":[OSD([subQ6])]})])],"derivedFrom":makeQuery(id+"F1.opExtrude","CAP_FACE",FACE,{"disambiguationData":[OSD([subQ6,subQ8,subQ9,subQ7,subQ4,subQ3,subQ2,subQ1,subQ0,subQ5,subQ10,subQ11])],"isStart":true})});}
            fillet(context, id + "F15", {"entities" : qUnion([Q0, Q1]), "radius" : 2 * mm, "tangentPropagation" : true, "allowEdgeOverflow" : false});
        }
    });
